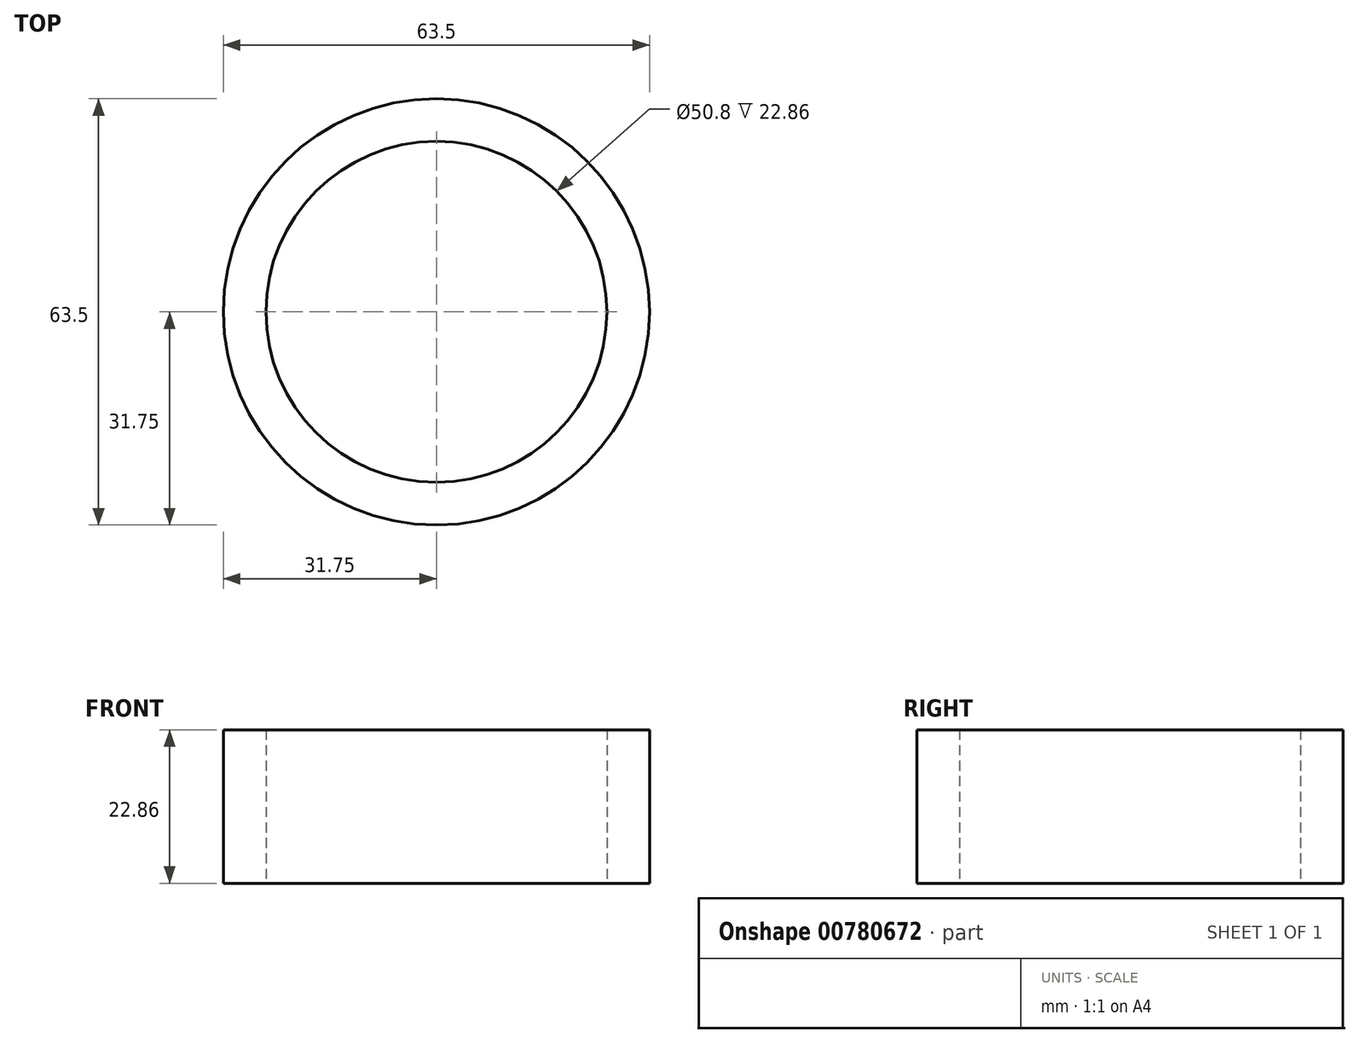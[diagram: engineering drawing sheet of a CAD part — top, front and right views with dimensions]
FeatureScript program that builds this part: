
annotation { "Feature Type Name" : "Feature", "Feature Type Description" : "" }
export const myFeature = defineFeature(function(context is Context, id is Id, definition is map)
    precondition{}
    {
        {
            var Q0;
            Q0=qCreatedBy(makeId("Top.planeOp"),FACE);
            var sketch = newSketch(context, id + "F0", { "sketchPlane" : qUnion([Q0])});
            skCircle(sketch, "E0", {"center": v(0, 0) * mm, "radius": 31.75 * mm});
            skCircle(sketch, "E1", {"center": v(0, 0) * mm, "radius": 25.4 * mm});
            skSolve(sketch);
        }
        {
            var Q0;
            Q0 = qSketchRegion(id + "F0", true);
            extrude(context, id + "F1", {"entities" : qUnion([Q0]), "depth" : 22.86 * mm, "offsetDistance" : 25.4 * mm});
        }
    });
